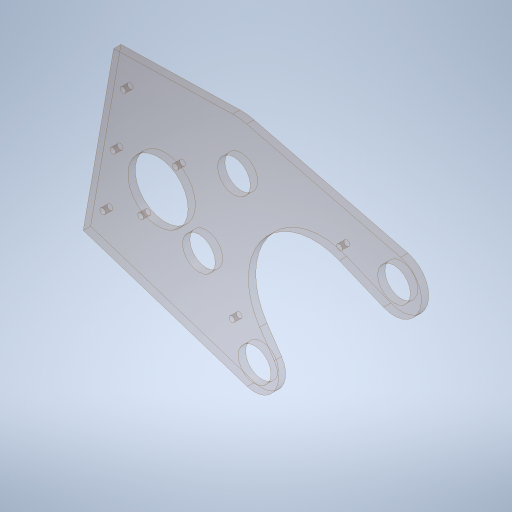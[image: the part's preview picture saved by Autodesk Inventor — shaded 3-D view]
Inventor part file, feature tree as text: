
AUTODESK INVENTOR PART (.ipt)
format: ipt  version: 2023.4 (Build 274418000, 418)  size: 352,256 bytes
history: native  units: in
note: dims shown in document units (in); Inventor stores cm internally (conversion verified against a paired STEP export)
features: sketch x1, extrude x1, hole x1
ambient origin geometry x8: Origin, YZ Plane, XZ Plane, XY Plane, X Axis, Y Axis, Z Axis, Center Point
bodies: Solid1 (feature_tree)
feature tree (3):
  sketch  "Sketch1"  dims[d3=45.0deg d4=0.0in d7=2.0in d8=4.25in d9=1.125in d10=3.0in d11=4.5in d12=4.5in d13=0.25in d14=0.375in d15=5.499in d16=1.128in d17=3.028in d18=3.126in d19=3.126in d22=1.0in d23=6.0in d26=8.0293in d27=2.0in d28=0.4688in d29=0.3504in d30=6.75in d31=0.0687in d32=0.75in d33=4.0in d34=1.375in d35=0.75in d36=0.25in d37=1.125in d38=2.3622in d40=360.0deg d43=0.1374in d44=0.375in d45=0.25in d46=0.0in d47=0.201in d48=0.75in d49=0.37in d50=0.25in d51=90.0deg d52=1.0in d53=0.8108in d54=0.3in d55=0.5497in d57=3.1875in d59=0.0312in]
  extrude  "Extrusion1"  TaperAngle=0.0deg  [1 undecoded]
  hole  "Hole1"  [1 undecoded]
note: 2 required parameter values undecoded (feature->parameter linkage not recoverable at this tier; creation-order binding heuristic only, values carry confidence <= 0.55)
